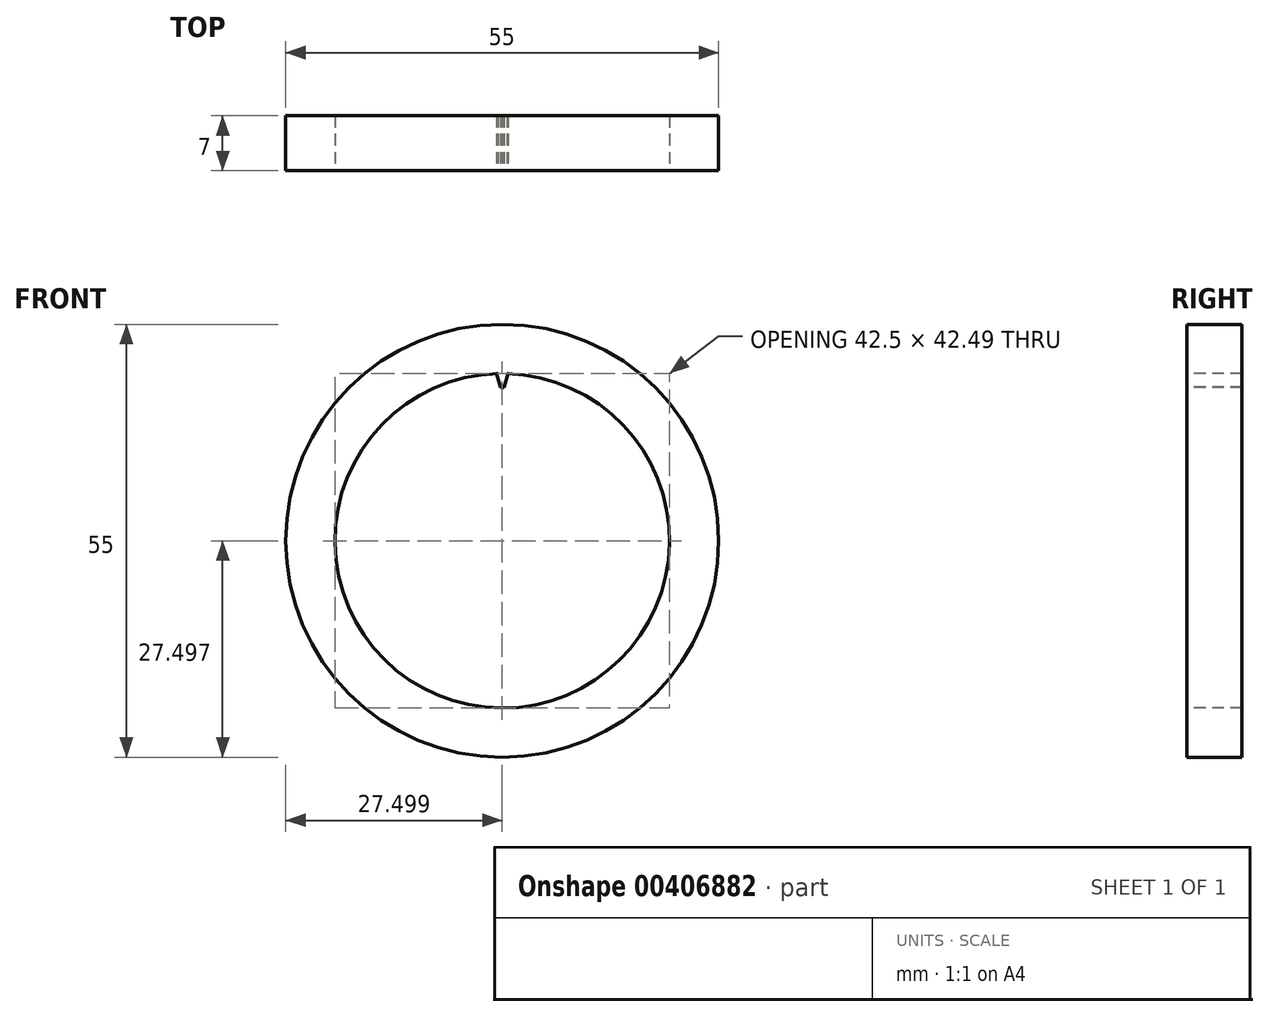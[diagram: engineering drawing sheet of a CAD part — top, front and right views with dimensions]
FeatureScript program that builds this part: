
annotation { "Feature Type Name" : "Feature", "Feature Type Description" : "" }
export const myFeature = defineFeature(function(context is Context, id is Id, definition is map)
    precondition{}
    {
        {
            var Q0;
            Q0=qCreatedBy(makeId("Front.planeOp"),FACE);
            var sketch = newSketch(context, id + "F0", { "sketchPlane" : qUnion([Q0])});
            skCircle(sketch, "E0", {"center": v(0, 0) * mm, "radius": 27.5 * mm});
            skSolve(sketch);
        }
        {
            var Q0;
            Q0 = qSketchRegion(id + "F0", true);
            var Q1;
            Q1=makeQuery(id+"F0.imprint","IMPRINT",FACE,{"disambiguationData":[TD([[makeQuery(id+"F0.imprint","IMPRINT",EDGE,{"derivedFrom":sQuery(id+"F0.wireOp",EDGE,"E0")}),1.0]])]});
            extrude(context, id + "F1", {"entities" : qUnion([Q0, Q1]), "endBound" : BoundingType.SYMMETRIC, "depth" : 7 * mm});
        }
        {
            var Q0;
            Q0=makeQuery(id+"F1.opExtrude","CAP_FACE",FACE,{"disambiguationData":[OSD([sQuery(id+"F0.wireOp",EDGE,"E0")])],"isStart":false});
            var sketch = newSketch(context, id + "F2", { "sketchPlane" : qUnion([Q0])});
            skCircle(sketch, "E1", {"center": v(0, 0) * mm, "radius": 21.25 * mm});
            skSolve(sketch);
        }
        {
            var Q0;
            Q0=makeQuery(id+"F2.imprint","IMPRINT",FACE,{"disambiguationData":[TD([[makeQuery(id+"F2.imprint","IMPRINT",EDGE,{"derivedFrom":sQuery(id+"F2.wireOp",EDGE,"E1")}),1.0]])]});
            extrude(context, id + "F3", {"entities" : qUnion([Q0]), "operationType" : NewBodyOperationType.REMOVE, "oppositeDirection" : true, "depth" : 25 * mm});
        }
        {
            var Q0;
            Q0=qCreatedBy(makeId("Front.planeOp"),FACE);
            var sketch = newSketch(context, id + "F4", { "sketchPlane" : qUnion([Q0])});
            skArc(sketch, "E2", {"start": v(0.21, 19.5) * mm, "mid": v(0, 19.5) * mm, "end": v(-0.21, 19.5) * mm});
            skLineSegment(sketch, "E3", {"start": v(-0.74, 21.23) * mm, "end": v(-0.21, 19.5) * mm});
            skLineSegment(sketch, "E4", {"start": v(0.21, 19.49) * mm, "end": v(0.76, 21.23) * mm});
            skPoint(sketch, "E5.orphan", {"position": v(-0.21, 19.5) * mm});
            skPoint(sketch, "E6.orphan", {"position": v(0.21, 19.5) * mm});
            skArc(sketch, "E7", {"start": v(0.21, 19.49) * mm, "mid": v(0, 19.5) * mm, "end": v(-0.21, 19.5) * mm});
            skArc(sketch, "E8", {"start": v(0.76, 21.23) * mm, "mid": v(0.01, 21.26) * mm, "end": v(-0.74, 21.23) * mm});
            skSolve(sketch);
        }
        {
            var Q0;
            {var subQ3=sQuery(id+"F4.wireOp",EDGE,"E8");Q0=makeQuery(id+"F4.imprint","IMPRINT",FACE,{"disambiguationData":[TD([[makeQuery(id+"F4.imprint","IMPRINT",EDGE,{"derivedFrom":subQ3}),1.0]])]});}
            extrude(context, id + "F5", {"entities" : qUnion([Q0]), "operationType" : NewBodyOperationType.ADD, "endBound" : BoundingType.SYMMETRIC, "oppositeDirection" : true, "depth" : 7 * mm});
        }
    });
